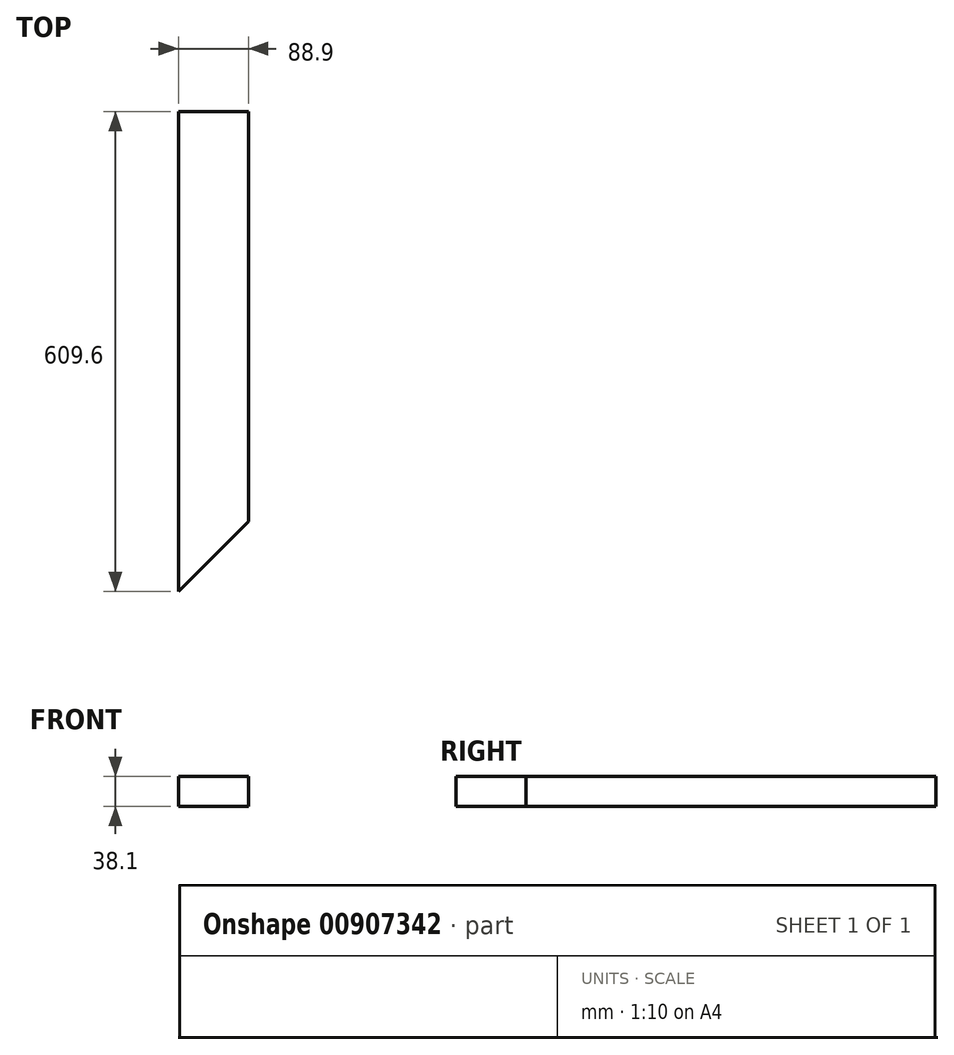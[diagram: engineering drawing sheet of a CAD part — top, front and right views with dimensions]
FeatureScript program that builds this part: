
annotation { "Feature Type Name" : "Feature", "Feature Type Description" : "" }
export const myFeature = defineFeature(function(context is Context, id is Id, definition is map)
    precondition{}
    {
        {
            var Q0;
            Q0=qCreatedBy(makeId("Front.planeOp"),FACE);
            var sketch = newSketch(context, id + "F0", { "sketchPlane" : qUnion([Q0])});
            skLineSegment(sketch, "E0.bottom", {"start": v(-44.45, 19.05) * mm, "end": v(44.45, 19.05) * mm});
            skLineSegment(sketch, "E0.top", {"start": v(-44.45, -19.05) * mm, "end": v(44.45, -19.05) * mm});
            skLineSegment(sketch, "E0.left", {"start": v(-44.45, 19.05) * mm, "end": v(-44.45, -19.05) * mm});
            skLineSegment(sketch, "E0.right", {"start": v(44.45, 19.05) * mm, "end": v(44.45, -19.05) * mm});
            skPoint(sketch, "E0.middle", {"position": v(0, 0) * mm});
            skSolve(sketch);
        }
        {
            var Q0;
            Q0=makeQuery(id+"F0.imprint","IMPRINT",FACE,{"disambiguationData":[TD([[makeQuery(id+"F0.imprint","IMPRINT",EDGE,{"derivedFrom":sQuery(id+"F0.wireOp",EDGE,"E0.bottom")}),-1.0]])]});
            extrude(context, id + "F1", {"entities" : qUnion([Q0]), "endBound" : BoundingType.SYMMETRIC, "depth" : 609.6 * mm, "offsetDistance" : 25.4 * mm});
        }
        {
            var Q0;
            Q0=makeQuery(id+"F1.opExtrude","CAP_EDGE",EDGE,{"disambiguationData":[OSD([sQuery(id+"F0.wireOp",EDGE,"E0.right")])],"isStart":false});
            chamfer(context, id + "F2", {"entities" : qUnion([Q0]), "chamferType" : ChamferType.TWO_OFFSETS, "width1" : 88.9 * mm, "oppositeDirection" : true, "width2" : 88.9 * mm, "tangentPropagation" : true});
        }
    });
